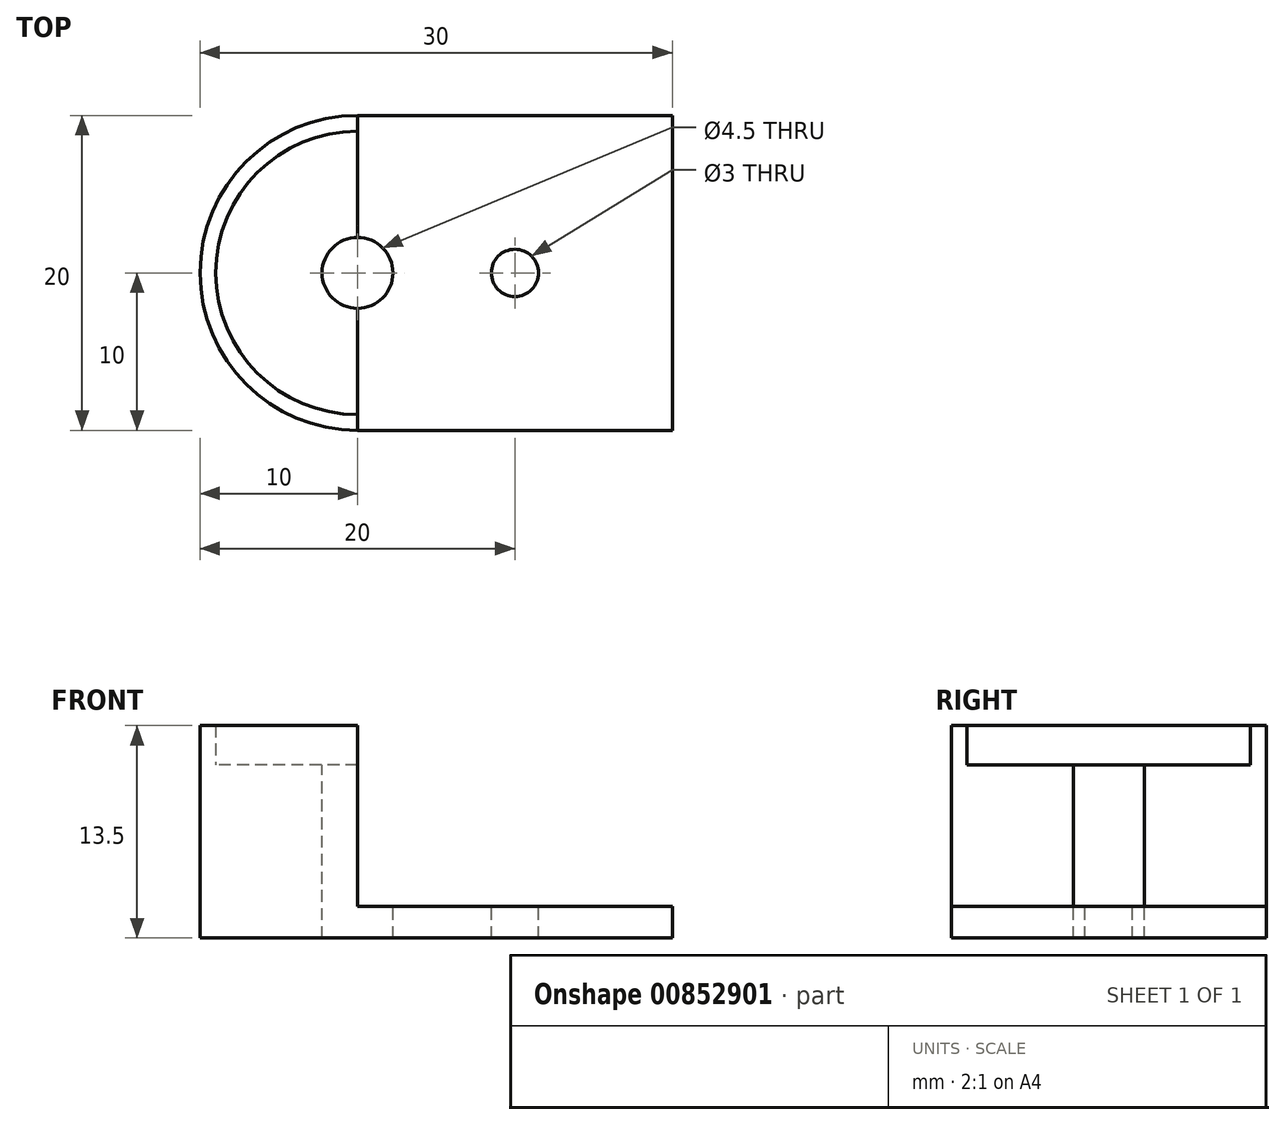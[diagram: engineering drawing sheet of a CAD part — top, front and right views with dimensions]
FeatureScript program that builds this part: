
annotation { "Feature Type Name" : "Feature", "Feature Type Description" : "" }
export const myFeature = defineFeature(function(context is Context, id is Id, definition is map)
    precondition{}
    {
        {
            var Q0;
            Q0=qCreatedBy(makeId("Top.planeOp"),FACE);
            var sketch = newSketch(context, id + "F0", { "sketchPlane" : qUnion([Q0])});
            skLineSegment(sketch, "E0.bottom", {"start": v(15, -10) * mm, "end": v(-5, -10) * mm});
            skLineSegment(sketch, "E0.top", {"start": v(15, 10) * mm, "end": v(-5, 10) * mm});
            skLineSegment(sketch, "E0.left", {"start": v(15, -10) * mm, "end": v(15, 10) * mm});
            skLineSegment(sketch, "E0.right", {"start": v(-15, 0) * mm, "end": v(-15, 0) * mm});
            skPoint(sketch, "E0.middle", {"position": v(0, 0) * mm});
            skLineSegment(sketch, "E1", {"start": v(-15, 0) * mm, "end": v(15, 0) * mm, "construction": true});
            skLineSegment(sketch, "E2", {"start": v(0, 0) * mm, "end": v(0, 10) * mm, "construction": true});
            skLineSegment(sketch, "E3", {"start": v(0, 10) * mm, "end": v(0, -10) * mm, "construction": true});
            skPoint(sketch, "E4.visualSharp", {"position": v(-15, 10) * mm});
            skArc(sketch, "E4.filletArc", {"start": v(-5, 10) * mm, "mid": v(-12.07, 7.07) * mm, "end": v(-15, 0) * mm});
            skPoint(sketch, "E5.visualSharp", {"position": v(-15, -10) * mm});
            skArc(sketch, "E5.filletArc", {"start": v(-15, 0) * mm, "mid": v(-12.07, -7.07) * mm, "end": v(-5, -10) * mm});
            skCircle(sketch, "E6", {"center": v(-5, 0) * mm, "radius": 2.25 * mm});
            skCircle(sketch, "E7", {"center": v(5, 0) * mm, "radius": 1.5 * mm});
            skLineSegment(sketch, "E8", {"start": v(-15, 10) * mm, "end": v(-15, -10) * mm, "construction": true});
            skArc(sketch, "E9.0", {"start": v(-5, 9) * mm, "mid": v(-11.36, 6.36) * mm, "end": v(-14, 0) * mm});
            skArc(sketch, "E10.0", {"start": v(-14, 0) * mm, "mid": v(-11.36, -6.36) * mm, "end": v(-5, -9) * mm});
            skLineSegment(sketch, "E11", {"start": v(-5, 9) * mm, "end": v(-5, 10) * mm});
            skLineSegment(sketch, "E12", {"start": v(-5, -10) * mm, "end": v(-5, -9) * mm});
            skLineSegment(sketch, "E13", {"start": v(-5, 9) * mm, "end": v(-5, 2.25) * mm});
            skLineSegment(sketch, "E14", {"start": v(-5, -9) * mm, "end": v(-5, -2.25) * mm});
            skSolve(sketch);
        }
        {
            var Q0;
            Q0 = qSketchRegion(id + "F0", true);
            var Q1;
            Q1=makeQuery(id+"F0.imprint","IMPRINT",FACE,{"disambiguationData":[TD([[makeQuery(id+"F0.imprint","IMPRINT",EDGE,{"derivedFrom":sQuery(id+"F0.wireOp",EDGE,"E9.0")}),1.0]])]});
            extrude(context, id + "F1", {"entities" : qUnion([Q0, Q1]), "oppositeDirection" : true, "depth" : 2 * mm, "offsetDistance" : 25 * mm});
        }
        {
            var Q0;
            Q0=makeQuery(id+"F0.imprint","IMPRINT",FACE,{"disambiguationData":[TD([[makeQuery(id+"F0.imprint","IMPRINT",EDGE,{"derivedFrom":sQuery(id+"F0.wireOp",EDGE,"E9.0")}),1.0]])]});
            var Q1;
            Q1=makeQuery(id+"F0.imprint","IMPRINT",FACE,{"disambiguationData":[TD([[makeQuery(id+"F0.imprint","IMPRINT",EDGE,{"derivedFrom":sQuery(id+"F0.wireOp",EDGE,"E4.filletArc")}),1.0]])]});
            extrude(context, id + "F2", {"entities" : qUnion([Q0, Q1]), "operationType" : NewBodyOperationType.ADD, "depth" : 9 * mm, "offsetDistance" : 25 * mm});
        }
        {
            var Q0;
            Q0=makeQuery(id+"F2.opExtrude","CAP_FACE",FACE,{"disambiguationData":[OSD([sQuery(id+"F0.wireOp",EDGE,"E4.filletArc"),sQuery(id+"F0.wireOp",EDGE,"E5.filletArc"),sQuery(id+"F0.wireOp",EDGE,"E6"),sQuery(id+"F0.wireOp",EDGE,"E11"),sQuery(id+"F0.wireOp",EDGE,"E12"),sQuery(id+"F0.wireOp",EDGE,"E13"),sQuery(id+"F0.wireOp",EDGE,"E14")])],"isStart":false});
            var sketch = newSketch(context, id + "F3", { "sketchPlane" : qUnion([Q0])});
            skArc(sketch, "E15.0", {"start": v(-5, 10) * mm, "mid": v(-12.07, 7.07) * mm, "end": v(-15, 0) * mm});
            skArc(sketch, "E16.0", {"start": v(-15, 0) * mm, "mid": v(-12.07, -7.07) * mm, "end": v(-5, -10) * mm});
            skArc(sketch, "E17.0", {"start": v(-14, 0) * mm, "mid": v(-11.36, -6.36) * mm, "end": v(-5, -9) * mm});
            skLineSegment(sketch, "E18.0", {"start": v(-5, -10) * mm, "end": v(-5, -9) * mm});
            skArc(sketch, "E19.0", {"start": v(-5, 9) * mm, "mid": v(-11.36, 6.36) * mm, "end": v(-14, 0) * mm});
            skLineSegment(sketch, "E20.0", {"start": v(-5, 9) * mm, "end": v(-5, 10) * mm});
            skSolve(sketch);
        }
        {
            var Q0;
            Q0 = qSketchRegion(id + "F3", true);
            extrude(context, id + "F4", {"entities" : qUnion([Q0]), "operationType" : NewBodyOperationType.ADD, "depth" : 2.5 * mm, "offsetDistance" : 25 * mm});
        }
    });
